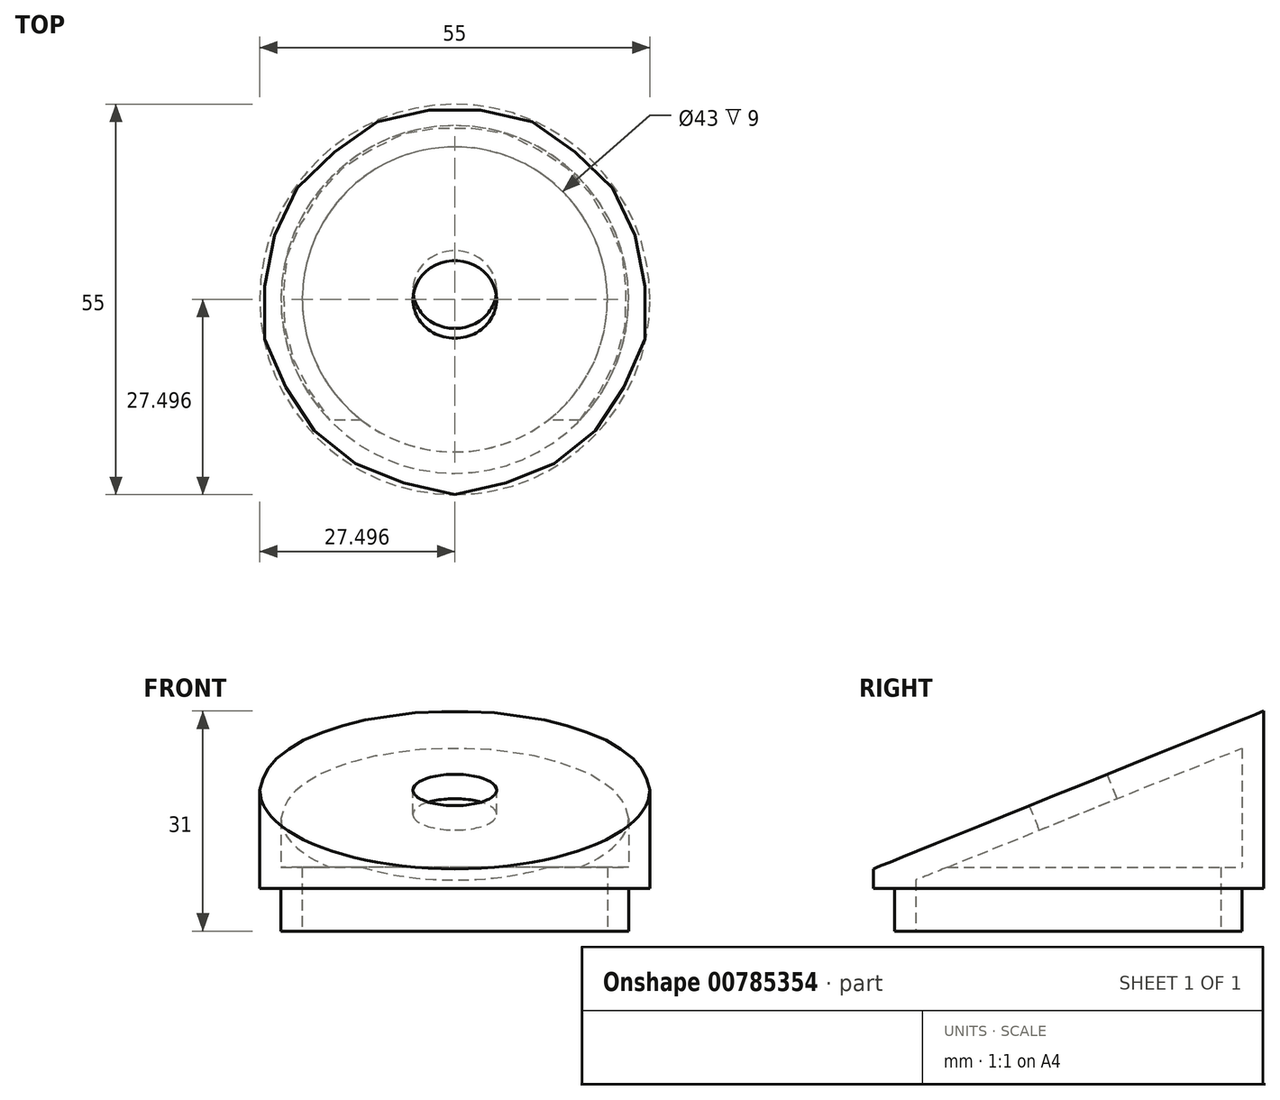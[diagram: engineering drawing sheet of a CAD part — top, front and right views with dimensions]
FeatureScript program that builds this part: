
annotation { "Feature Type Name" : "Feature", "Feature Type Description" : "" }
export const myFeature = defineFeature(function(context is Context, id is Id, definition is map)
    precondition{}
    {
        {
            var Q0;
            Q0=qCreatedBy(makeId("Top.planeOp"),FACE);
            var sketch = newSketch(context, id + "F0", { "sketchPlane" : qUnion([Q0])});
            skCircle(sketch, "E0", {"center": v(-46.3, 17.49) * mm, "radius": 24.5 * mm});
            skCircle(sketch, "E1.0", {"center": v(-46.3, 17.49) * mm, "radius": 27.5 * mm});
            skCircle(sketch, "E2.0", {"center": v(-46.3, 17.49) * mm, "radius": 21.5 * mm});
            skSolve(sketch);
        }
        {
            var Q0;
            Q0=makeQuery(id+"F0.imprint","IMPRINT",FACE,{"disambiguationData":[TD([[makeQuery(id+"F0.imprint","IMPRINT",EDGE,{"derivedFrom":sQuery(id+"F0.wireOp",EDGE,"E0")}),-1.0]])]});
            extrude(context, id + "F1", {"entities" : qUnion([Q0]), "depth" : 25 * mm, "offsetDistance" : 25 * mm});
        }
        {
            var Q0;
            Q0=qCreatedBy(makeId("Right.planeOp"),FACE);
            var sketch = newSketch(context, id + "F2", { "sketchPlane" : qUnion([Q0])});
            skLineSegment(sketch, "E3.0", {"start": v(-10.01, 25) * mm, "end": v(44.99, 25) * mm});
            skLineSegment(sketch, "E3.1", {"start": v(-10.01, 0) * mm, "end": v(44.99, 0) * mm});
            skLineSegment(sketch, "E4", {"start": v(44.99, 25) * mm, "end": v(44.99, 0) * mm});
            skLineSegment(sketch, "E5", {"start": v(-10.01, 25) * mm, "end": v(-10.01, 0) * mm});
            skLineSegment(sketch, "E6", {"start": v(44.99, 25) * mm, "end": v(-10.01, 2.76) * mm});
            skSolve(sketch);
        }
        {
            var Q0;
            {var subQ0=sQuery(id+"F2.wireOp",EDGE,"E3.0");Q0=makeQuery(id+"F2.imprint","IMPRINT",FACE,{"disambiguationData":[TD([[makeQuery(id+"F2.imprint","IMPRINT",EDGE,{"derivedFrom":subQ0}),-1.0]])]});}
            extrude(context, id + "F3", {"entities" : qUnion([Q0]), "operationType" : NewBodyOperationType.REMOVE, "oppositeDirection" : true, "depth" : 82.3 * mm, "offsetDistance" : 25 * mm});
        }
        {
            var Q0;
            Q0=makeQuery(id+"F3.boolean.opBoolean","COPY",FACE,{"derivedFrom":makeQuery(id+"F3.opExtrude","SWEPT_FACE",FACE,{"disambiguationData":[OSD([sQuery(id+"F2.wireOp",EDGE,"E6")])]})});
            var sketch = newSketch(context, id + "F4", { "sketchPlane" : qUnion([Q0])});
            skSolve(sketch);
        }
        {
            var Q0;
            Q0=qCreatedBy(makeId("Front.planeOp"),FACE);
            var sketch = newSketch(context, id + "F5", { "sketchPlane" : qUnion([Q0])});
            skLineSegment(sketch, "E7.0", {"start": v(-73.8, 0) * mm, "end": v(-18.8, 0) * mm});
            skLineSegment(sketch, "E8", {"start": v(-46.3, 4) * mm, "end": v(-46.3, 0) * mm});
            skPoint(sketch, "E8.startSnap0", {"position": v(-46.3, 0) * mm});
            skPoint(sketch, "E9.orphan", {"position": v(-46.3, 26.65) * mm});
            skEllipse(sketch, "E10.0", {"center": v(-46.3, 13.88) * mm, "majorRadius": 24.5 * mm, "minorRadius": 9.9 * mm, "majorAxis": v(1, 0)});
            skSolve(sketch);
        }
        {
            var Q0;
            Q0=makeQuery(id+"F4.imprint","IMPRINT",FACE,{"disambiguationData":[TD([[makeQuery(id+"F4.imprint","IMPRINT",EDGE,{"derivedFrom":makeQuery(id+"F3.boolean.opBoolean","INTERSECT",EDGE,{"derivedFrom":[makeQuery(id+"F1.opExtrude","SWEPT_FACE",FACE,{"disambiguationData":[OSD([sQuery(id+"F0.wireOp",EDGE,"E0")])]}),makeQuery(id+"F3.opExtrude","SWEPT_FACE",FACE,{"disambiguationData":[OSD([sQuery(id+"F2.wireOp",EDGE,"E6")])]})]})}),1.0]])]});
            var Q1;
            Q1=sQuery(id+"F5.wireOp",EDGE,"E8");
            sweep(context, id + "F6", {"operationType" : NewBodyOperationType.ADD, "profiles" : qUnion([Q0]), "path" : qUnion([Q1])});
        }
        {
            var Q0;
            Q0=makeQuery(id+"F0.imprint","IMPRINT",FACE,{"disambiguationData":[TD([[makeQuery(id+"F0.imprint","IMPRINT",EDGE,{"derivedFrom":sQuery(id+"F0.wireOp",EDGE,"E0")}),1.0]])]});
            extrude(context, id + "F7", {"entities" : qUnion([Q0]), "operationType" : NewBodyOperationType.ADD, "depth" : 3 * mm, "offsetDistance" : 25 * mm});
        }
        {
            var Q0;
            Q0=makeQuery(id+"F0.imprint","IMPRINT",FACE,{"disambiguationData":[TD([[makeQuery(id+"F0.imprint","IMPRINT",EDGE,{"derivedFrom":sQuery(id+"F0.wireOp",EDGE,"E0")}),1.0]])]});
            extrude(context, id + "F8", {"entities" : qUnion([Q0]), "operationType" : NewBodyOperationType.ADD, "oppositeDirection" : true, "depth" : 6 * mm, "offsetDistance" : 25 * mm});
        }
        {
            var Q0;
            {var subQ0=sQuery(id+"F2.wireOp",EDGE,"E6");Q0=makeQuery(id+"F6.boolean.opBoolean","MERGE",FACE,{"derivedFrom":[makeQuery(id+"F3.boolean.opBoolean","COPY",FACE,{"derivedFrom":makeQuery(id+"F3.opExtrude","SWEPT_FACE",FACE,{"disambiguationData":[OSD([subQ0])]})}),makeQuery(id+"F6.opSweep","CAP_FACE",FACE,{"disambiguationData":[OSD([sQuery(id+"F0.wireOp",EDGE,"E0"),subQ0,sQuery(id+"F5.wireOp",VERTEX,"E8.start")])],"isStart":true})]});}
            var sketch = newSketch(context, id + "F9", { "sketchPlane" : qUnion([Q0])});
            skEllipse(sketch, "E11.0", {"center": v(-46.3, 21.41) * mm, "majorRadius": 29.66 * mm, "minorRadius": 27.5 * mm, "majorAxis": v(0, -1)});
            skCircle(sketch, "E12", {"center": v(-46.3, 21.41) * mm, "radius": 5.9 * mm});
            skSolve(sketch);
        }
        {
            var Q0;
            Q0=makeQuery(id+"F9.imprint","IMPRINT",FACE,{"disambiguationData":[TD([[makeQuery(id+"F9.imprint","IMPRINT",EDGE,{"derivedFrom":sQuery(id+"F9.wireOp",EDGE,"E12")}),1.0]])]});
            extrude(context, id + "F10", {"entities" : qUnion([Q0]), "operationType" : NewBodyOperationType.REMOVE, "oppositeDirection" : true, "depth" : 12.8 * mm, "offsetDistance" : 25 * mm});
        }
    });
